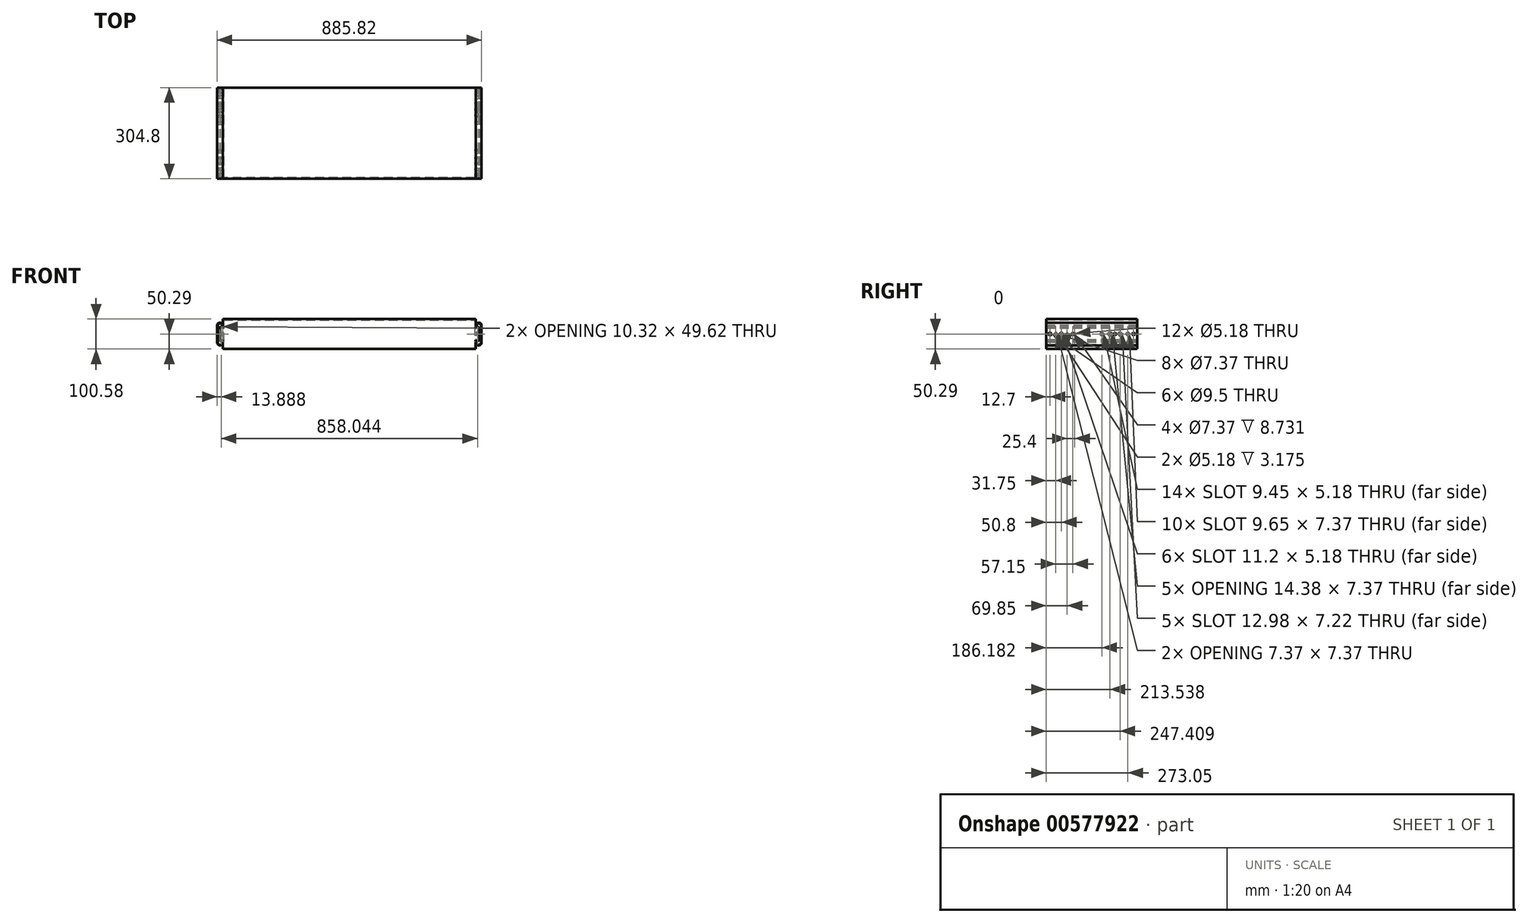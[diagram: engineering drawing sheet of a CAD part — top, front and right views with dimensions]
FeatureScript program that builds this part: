
annotation { "Feature Type Name" : "Feature", "Feature Type Description" : "" }
export const myFeature = defineFeature(function(context is Context, id is Id, definition is map)
    precondition{}
    {
        {
            var Q0;
            Q0=qCreatedBy(makeId("Front.planeOp"),FACE);
            var sketch = newSketch(context, id + "F0", { "sketchPlane" : qUnion([Q0])});
            skLineSegment(sketch, "E0", {"start": v(-442.91, 0) * mm, "end": v(442.91, 0) * mm, "construction": true});
            skLineSegment(sketch, "E1", {"start": v(-442.91, 9.53) * mm, "end": v(-442.91, 66.67) * mm});
            skArc(sketch, "E2", {"start": v(-442.91, 9.53) * mm, "mid": v(-433.39, 0) * mm, "end": v(-423.86, 9.53) * mm});
            skArc(sketch, "E3", {"start": v(-423.86, 66.67) * mm, "mid": v(-433.39, 76.2) * mm, "end": v(-442.91, 66.67) * mm});
            skLineSegment(sketch, "E4", {"start": v(-424.7, 66.67) * mm, "end": v(-423.86, 66.67) * mm, "construction": true});
            skLineSegment(sketch, "E5", {"start": v(-442.91, 9.53) * mm, "end": v(-423.86, 9.53) * mm, "construction": true});
            skArc(sketch, "E6.0", {"start": v(-441.33, 9.53) * mm, "mid": v(-433.75, 1.6) * mm, "end": v(-425.48, 8.8) * mm});
            skLineSegment(sketch, "E6.1", {"start": v(-441.33, 9.53) * mm, "end": v(-441.33, 66.67) * mm});
            skArc(sketch, "E6.2", {"start": v(-425.48, 67.4) * mm, "mid": v(-433.75, 74.6) * mm, "end": v(-441.33, 66.67) * mm});
            skLineSegment(sketch, "E7", {"start": v(-424.7, 9.53) * mm, "end": v(-423.86, 9.53) * mm});
            skLineSegment(sketch, "E8", {"start": v(-425.45, 66.67) * mm, "end": v(-423.86, 66.67) * mm});
            skArc(sketch, "E9.0", {"start": v(-440.53, 9.52) * mm, "mid": v(-433.39, 2.38) * mm, "end": v(-426.24, 9.53) * mm});
            skLineSegment(sketch, "E9.1", {"start": v(-440.53, 9.52) * mm, "end": v(-440.53, 66.67) * mm});
            skArc(sketch, "E9.2", {"start": v(-426.24, 66.67) * mm, "mid": v(-433.39, 73.82) * mm, "end": v(-440.53, 66.67) * mm});
            skLineSegment(sketch, "E10", {"start": v(-426.24, 66.67) * mm, "end": v(-426.24, 66.67) * mm});
            skLineSegment(sketch, "E11", {"start": v(-422.28, 56.97) * mm, "end": v(-422.28, 19.23) * mm, "construction": true});
            skLineSegment(sketch, "E12", {"start": v(-422.28, 10.32) * mm, "end": v(-425.45, 10.32) * mm});
            skLineSegment(sketch, "E13", {"start": v(-426.24, 9.53) * mm, "end": v(-426.24, 9.53) * mm});
            skLineSegment(sketch, "E14", {"start": v(-434.18, 19.23) * mm, "end": v(-434.18, 56.97) * mm});
            skArc(sketch, "E15", {"start": v(-422.28, 56.97) * mm, "mid": v(-428.23, 62.92) * mm, "end": v(-434.18, 56.97) * mm});
            skArc(sketch, "E16", {"start": v(-434.18, 19.23) * mm, "mid": v(-428.23, 13.28) * mm, "end": v(-422.28, 19.23) * mm});
            skLineSegment(sketch, "E17", {"start": v(-440.53, 38.1) * mm, "end": v(-434.18, 38.1) * mm, "construction": true});
            skLineSegment(sketch, "E18", {"start": v(-425.45, 65.88) * mm, "end": v(-423.86, 65.88) * mm});
            skArc(sketch, "E19.0", {"start": v(-432.6, 19.23) * mm, "mid": v(-428.23, 14.86) * mm, "end": v(-423.86, 19.23) * mm});
            skLineSegment(sketch, "E19.1", {"start": v(-432.6, 19.23) * mm, "end": v(-432.6, 56.97) * mm});
            skArc(sketch, "E19.2", {"start": v(-423.86, 56.97) * mm, "mid": v(-428.23, 61.34) * mm, "end": v(-432.6, 56.97) * mm});
            skLineSegment(sketch, "E20", {"start": v(-423.86, 56.97) * mm, "end": v(-423.86, 19.23) * mm});
            skLineSegment(sketch, "E21", {"start": v(-423.86, 10.32) * mm, "end": v(-423.86, 15.18) * mm});
            skLineSegment(sketch, "E22", {"start": v(-423.86, 65.88) * mm, "end": v(-423.86, 61.02) * mm});
            skPoint(sketch, "E23.visualSharp", {"position": v(-426.24, 65.88) * mm});
            skArc(sketch, "E23.filletArc", {"start": v(-426.24, 66.67) * mm, "mid": v(-426.01, 66.11) * mm, "end": v(-425.45, 65.88) * mm});
            skArc(sketch, "E24.filletArc", {"start": v(-425.48, 67.4) * mm, "mid": v(-425.23, 66.88) * mm, "end": v(-424.7, 66.68) * mm});
            skPoint(sketch, "E25.visualSharp", {"position": v(-425.45, 9.53) * mm});
            skArc(sketch, "E25.filletArc", {"start": v(-424.7, 9.53) * mm, "mid": v(-425.23, 9.32) * mm, "end": v(-425.48, 8.8) * mm});
            skPoint(sketch, "E26.visualSharp", {"position": v(-426.24, 10.32) * mm});
            skArc(sketch, "E26.filletArc", {"start": v(-425.45, 10.32) * mm, "mid": v(-426.01, 10.09) * mm, "end": v(-426.24, 9.53) * mm});
            skSolve(sketch);
        }
        {
            var Q0;
            Q0 = qSketchRegion(id + "F0", true);
            extrude(context, id + "F1", {"entities" : qUnion([Q0]), "oppositeDirection" : true, "depth" : 304.8 * mm, "offsetDistance" : 25.4 * mm});
        }
        {
            var Q0;
            Q0=makeQuery(id+"F1.opExtrude","SWEPT_FACE",FACE,{"disambiguationData":[OSD([sQuery(id+"F0.wireOp",EDGE,"E20")])]});
            var sketch = newSketch(context, id + "F2", { "sketchPlane" : qUnion([Q0])});
            skPoint(sketch, "E27", {"position": v(304.8, 38.1) * mm});
            skLineSegment(sketch, "E28", {"start": v(50.8, 35.1) * mm, "end": v(50.8, 41.1) * mm});
            skLineSegment(sketch, "E29", {"start": v(208.94, 38.1) * mm, "end": v(213.2, 38.1) * mm});
            skLineSegment(sketch, "E30", {"start": v(228, 38.1) * mm, "end": v(232.26, 38.1) * mm});
            skLineSegment(sketch, "E31", {"start": v(251.3, 38.1) * mm, "end": v(247.04, 38.1) * mm});
            skPoint(sketch, "E32", {"position": v(50.8, 38.1) * mm});
            skArc(sketch, "E33.0.startCap", {"start": v(53.4, 35.1) * mm, "mid": v(50.8, 32.5) * mm, "end": v(48.2, 35.1) * mm});
            skArc(sketch, "E33.0.endCap", {"start": v(48.2, 41.1) * mm, "mid": v(50.8, 43.7) * mm, "end": v(53.4, 41.1) * mm});
            skLineSegment(sketch, "E33.0.left", {"start": v(48.2, 35.1) * mm, "end": v(48.2, 41.1) * mm});
            skLineSegment(sketch, "E33.0.right", {"start": v(53.4, 35.1) * mm, "end": v(53.4, 41.1) * mm});
            skLineSegment(sketch, "E34", {"start": v(188.32, 38.1) * mm, "end": v(184.05, 38.1) * mm});
            skArc(sketch, "E35.0.startCap", {"start": v(188.32, 40.7) * mm, "mid": v(190.9, 38.1) * mm, "end": v(188.32, 35.5) * mm});
            skArc(sketch, "E35.0.endCap", {"start": v(184.05, 35.5) * mm, "mid": v(181.46, 38.1) * mm, "end": v(184.05, 40.7) * mm});
            skLineSegment(sketch, "E35.0.left", {"start": v(188.32, 35.5) * mm, "end": v(184.05, 35.5) * mm});
            skLineSegment(sketch, "E35.0.right", {"start": v(188.32, 40.7) * mm, "end": v(184.05, 40.7) * mm});
            skArc(sketch, "E35.1.startCap", {"start": v(208.94, 35.5) * mm, "mid": v(206.35, 38.1) * mm, "end": v(208.94, 40.7) * mm});
            skArc(sketch, "E35.1.endCap", {"start": v(213.2, 40.7) * mm, "mid": v(215.8, 38.1) * mm, "end": v(213.2, 35.5) * mm});
            skLineSegment(sketch, "E35.1.left", {"start": v(208.94, 40.7) * mm, "end": v(213.2, 40.7) * mm});
            skLineSegment(sketch, "E35.1.right", {"start": v(208.94, 35.5) * mm, "end": v(213.2, 35.5) * mm});
            skArc(sketch, "E35.2.startCap", {"start": v(228, 35.5) * mm, "mid": v(225.4, 38.1) * mm, "end": v(228, 40.7) * mm});
            skArc(sketch, "E35.2.endCap", {"start": v(232.26, 40.7) * mm, "mid": v(234.85, 38.1) * mm, "end": v(232.26, 35.5) * mm});
            skLineSegment(sketch, "E35.2.left", {"start": v(228, 40.7) * mm, "end": v(232.26, 40.7) * mm});
            skLineSegment(sketch, "E35.2.right", {"start": v(228, 35.5) * mm, "end": v(232.26, 35.5) * mm});
            skArc(sketch, "E35.3.startCap", {"start": v(251.3, 40.7) * mm, "mid": v(253.9, 38.1) * mm, "end": v(251.3, 35.5) * mm});
            skArc(sketch, "E35.3.endCap", {"start": v(247.04, 35.5) * mm, "mid": v(244.45, 38.1) * mm, "end": v(247.04, 40.7) * mm});
            skLineSegment(sketch, "E35.3.left", {"start": v(251.3, 35.5) * mm, "end": v(247.04, 35.5) * mm});
            skLineSegment(sketch, "E35.3.right", {"start": v(251.3, 40.7) * mm, "end": v(247.04, 40.7) * mm});
            skPoint(sketch, "E36", {"position": v(186.18, 38.1) * mm});
            skPoint(sketch, "E37", {"position": v(211.07, 38.1) * mm});
            skPoint(sketch, "E38", {"position": v(230.12, 38.1) * mm});
            skPoint(sketch, "E39", {"position": v(249.17, 38.1) * mm});
            skCircle(sketch, "E40", {"center": v(31.75, 38.1) * mm, "radius": 2.6 * mm});
            skCircle(sketch, "E41", {"center": v(69.85, 38.1) * mm, "radius": 2.6 * mm});
            skCircle(sketch, "E42", {"center": v(95.25, 38.1) * mm, "radius": 2.6 * mm});
            skCircle(sketch, "E43", {"center": v(12.7, 38.1) * mm, "radius": 4.75 * mm});
            skSolve(sketch);
        }
        {
            var Q0;
            Q0 = qSketchRegion(id + "F2", true);
            extrude(context, id + "F3", {"entities" : qUnion([Q0]), "operationType" : NewBodyOperationType.REMOVE, "oppositeDirection" : true, "depth" : 25.4 * mm, "offsetDistance" : 25.4 * mm});
        }
        {
            var Q0;
            Q0=makeQuery(id+"F1.opExtrude","SWEPT_FACE",FACE,{"disambiguationData":[OSD([sQuery(id+"F0.wireOp",EDGE,"E1")])]});
            var sketch = newSketch(context, id + "F4", { "sketchPlane" : qUnion([Q0])});
            skCircle(sketch, "E44", {"center": v(-88.9, 38.1) * mm, "radius": 3.68 * mm});
            skPoint(sketch, "E44.centerSnap0", {"position": v(0, 38.1) * mm});
            skCircle(sketch, "E45", {"center": v(-31.75, 38.1) * mm, "radius": 3.68 * mm});
            skCircle(sketch, "E46", {"center": v(-244.6, 38.1) * mm, "radius": 3.68 * mm});
            skLineSegment(sketch, "E47", {"start": v(-293.24, 38.1) * mm, "end": v(-290.96, 38.1) * mm});
            skPoint(sketch, "E47.startSnap0", {"position": v(-304.8, 38.1) * mm});
            skLineSegment(sketch, "E48", {"start": v(-274.2, 38.1) * mm, "end": v(-271.9, 38.1) * mm});
            skLineSegment(sketch, "E49", {"start": v(-217.04, 38.1) * mm, "end": v(-214.76, 38.1) * mm});
            skPoint(sketch, "E50", {"position": v(-292.1, 38.1) * mm});
            skPoint(sketch, "E51", {"position": v(-273.05, 38.1) * mm});
            skPoint(sketch, "E52", {"position": v(-215.9, 38.1) * mm});
            skArc(sketch, "E53.0.startCap", {"start": v(-293.24, 34.42) * mm, "mid": v(-296.93, 38.1) * mm, "end": v(-293.24, 41.78) * mm});
            skArc(sketch, "E53.0.endCap", {"start": v(-290.96, 41.78) * mm, "mid": v(-287.27, 38.1) * mm, "end": v(-290.96, 34.42) * mm});
            skLineSegment(sketch, "E53.0.left", {"start": v(-293.24, 41.78) * mm, "end": v(-290.96, 41.78) * mm});
            skLineSegment(sketch, "E53.0.right", {"start": v(-293.24, 34.42) * mm, "end": v(-290.96, 34.42) * mm});
            skArc(sketch, "E53.1.startCap", {"start": v(-274.2, 34.42) * mm, "mid": v(-277.88, 38.1) * mm, "end": v(-274.2, 41.78) * mm});
            skArc(sketch, "E53.1.endCap", {"start": v(-271.9, 41.78) * mm, "mid": v(-268.22, 38.1) * mm, "end": v(-271.9, 34.42) * mm});
            skLineSegment(sketch, "E53.1.left", {"start": v(-274.2, 41.78) * mm, "end": v(-271.9, 41.78) * mm});
            skLineSegment(sketch, "E53.1.right", {"start": v(-274.2, 34.42) * mm, "end": v(-271.9, 34.42) * mm});
            skArc(sketch, "E53.2.startCap", {"start": v(-217.04, 34.42) * mm, "mid": v(-220.73, 38.1) * mm, "end": v(-217.04, 41.78) * mm});
            skArc(sketch, "E53.2.endCap", {"start": v(-214.76, 41.78) * mm, "mid": v(-211.07, 38.1) * mm, "end": v(-214.76, 34.42) * mm});
            skLineSegment(sketch, "E53.2.left", {"start": v(-217.04, 41.78) * mm, "end": v(-214.76, 41.78) * mm});
            skLineSegment(sketch, "E53.2.right", {"start": v(-217.04, 34.42) * mm, "end": v(-214.76, 34.42) * mm});
            skSolve(sketch);
        }
        {
            var Q0;
            Q0 = qSketchRegion(id + "F4", true);
            extrude(context, id + "F5", {"entities" : qUnion([Q0]), "operationType" : NewBodyOperationType.REMOVE, "oppositeDirection" : true, "depth" : 25.4 * mm, "offsetDistance" : 25.4 * mm});
        }
        {
            var Q0;
            Q0=makeQuery(id+"F1.opExtrude","CAP_FACE",FACE,{"disambiguationData":[OSD([sQuery(id+"F0.wireOp",EDGE,"E19.0"),sQuery(id+"F0.wireOp",EDGE,"E19.1"),sQuery(id+"F0.wireOp",EDGE,"E19.2"),sQuery(id+"F0.wireOp",EDGE,"E20")])],"isStart":true});
            extrude(context, id + "F6", {"entities" : qUnion([Q0]), "operationType" : NewBodyOperationType.REMOVE, "oppositeDirection" : true, "depth" : 3.17 * mm, "offsetDistance" : 25.4 * mm});
        }
        {
            var Q0;
            Q0=makeQuery(id+"F6.boolean.opBoolean","COPY",FACE,{"derivedFrom":makeQuery(id+"F6.opExtrude","CAP_FACE",FACE,{"disambiguationData":[OSD([sQuery(id+"F0.wireOp",EDGE,"E19.0"),sQuery(id+"F0.wireOp",EDGE,"E19.1"),sQuery(id+"F0.wireOp",EDGE,"E19.2"),sQuery(id+"F0.wireOp",EDGE,"E20")])],"isStart":false})});
            extrude(context, id + "F7", {"entities" : qUnion([Q0]), "depth" : 3.17 * mm, "offsetDistance" : 25.4 * mm});
        }
        {
            var Q0;
            Q0=makeQuery(id+"F1.opExtrude","SWEPT_BODY",BODY,{"disambiguationData":[OSD([sQuery(id+"F0.wireOp",EDGE,"E19.0"),sQuery(id+"F0.wireOp",EDGE,"E19.1"),sQuery(id+"F0.wireOp",EDGE,"E19.2"),sQuery(id+"F0.wireOp",EDGE,"E20")])]});
            var Q1;
            Q1=makeQuery(id+"F1.opExtrude","SWEPT_BODY",BODY,{"disambiguationData":[OSD([sQuery(id+"F0.wireOp",EDGE,"E9.0"),sQuery(id+"F0.wireOp",EDGE,"E9.1"),sQuery(id+"F0.wireOp",EDGE,"E9.2"),sQuery(id+"F0.wireOp",EDGE,"E12"),sQuery(id+"F0.wireOp",EDGE,"E14"),sQuery(id+"F0.wireOp",EDGE,"E15"),sQuery(id+"F0.wireOp",EDGE,"E16"),sQuery(id+"F0.wireOp",EDGE,"E18"),sQuery(id+"F0.wireOp",EDGE,"E21"),sQuery(id+"F0.wireOp",EDGE,"E22"),sQuery(id+"F0.wireOp",EDGE,"E23.filletArc"),sQuery(id+"F0.wireOp",EDGE,"E26.filletArc")])]});
            var Q2;
            Q2=makeQuery(id+"F1.opExtrude","SWEPT_BODY",BODY,{"disambiguationData":[OSD([sQuery(id+"F0.wireOp",EDGE,"E1"),sQuery(id+"F0.wireOp",EDGE,"E2"),sQuery(id+"F0.wireOp",EDGE,"E3"),sQuery(id+"F0.wireOp",EDGE,"E6.0"),sQuery(id+"F0.wireOp",EDGE,"E6.1"),sQuery(id+"F0.wireOp",EDGE,"E6.2"),sQuery(id+"F0.wireOp",EDGE,"E7"),sQuery(id+"F0.wireOp",EDGE,"E8"),sQuery(id+"F0.wireOp",EDGE,"E24.filletArc"),sQuery(id+"F0.wireOp",EDGE,"E25.filletArc")])]});
            var Q3;
            Q3=makeQuery(id+"F7.opExtrude","SWEPT_BODY",BODY,{"disambiguationData":[OSD([sQuery(id+"F0.wireOp",EDGE,"E19.0"),sQuery(id+"F0.wireOp",EDGE,"E19.1"),sQuery(id+"F0.wireOp",EDGE,"E19.2"),sQuery(id+"F0.wireOp",EDGE,"E20")])]});
            var Q4;
            Q4=qCreatedBy(makeId("Right.planeOp"),FACE);
            mirror(context, id + "F8", {"entities" : qUnion([Q0, Q1, Q2, Q3]), "mirrorPlane" : qUnion([Q4])});
        }
        {
            var Q0;
            Q0=qCreatedBy(makeId("Front.planeOp"),FACE);
            var sketch = newSketch(context, id + "F9", { "sketchPlane" : qUnion([Q0])});
            skLineSegment(sketch, "E54.bottom", {"start": v(-423.86, 88.4) * mm, "end": v(-420.69, 88.4) * mm});
            skLineSegment(sketch, "E54.top", {"start": v(-423.86, -12.2) * mm, "end": v(-420.69, -12.2) * mm});
            skLineSegment(sketch, "E54.right", {"start": v(-420.69, 88.4) * mm, "end": v(-420.69, -12.2) * mm});
            skLineSegment(sketch, "E55.top", {"start": v(-423.86, -9.02) * mm, "end": v(-420.69, -9.02) * mm});
            skLineSegment(sketch, "E55.left", {"start": v(-423.86, -12.2) * mm, "end": v(-423.86, -9.02) * mm});
            skLineSegment(sketch, "E55.right", {"start": v(423.86, -12.2) * mm, "end": v(423.86, -9.02) * mm});
            skLineSegment(sketch, "E56.bottom", {"start": v(423.86, -12.2) * mm, "end": v(420.69, -12.2) * mm});
            skLineSegment(sketch, "E56.top", {"start": v(423.86, 88.4) * mm, "end": v(420.69, 88.4) * mm});
            skLineSegment(sketch, "E56.left", {"start": v(423.86, -12.2) * mm, "end": v(423.86, 88.4) * mm});
            skLineSegment(sketch, "E56.right", {"start": v(420.69, -12.2) * mm, "end": v(420.69, 88.4) * mm});
            skLineSegment(sketch, "E57", {"start": v(-423.86, 88.4) * mm, "end": v(-423.86, -12.2) * mm});
            skLineSegment(sketch, "E58.0.0", {"start": v(-423.86, 19.23) * mm, "end": v(-423.86, 56.97) * mm});
            skLineSegment(sketch, "E58.0.2", {"start": v(-432.6, 56.97) * mm, "end": v(-432.6, 19.23) * mm});
            skArc(sketch, "E58.0.3", {"start": v(-432.6, 19.23) * mm, "mid": v(-428.23, 14.86) * mm, "end": v(-423.86, 19.23) * mm});
            skPoint(sketch, "E59", {"position": v(-423.86, 38.1) * mm});
            skLineSegment(sketch, "E60.bottom", {"start": v(-423.86, 88.4) * mm, "end": v(423.86, 88.4) * mm});
            skLineSegment(sketch, "E60.top", {"start": v(-423.86, 85.22) * mm, "end": v(423.86, 85.22) * mm});
            skLineSegment(sketch, "E60.left", {"start": v(-423.86, 88.4) * mm, "end": v(-423.86, 85.22) * mm});
            skLineSegment(sketch, "E60.right", {"start": v(423.86, 88.4) * mm, "end": v(423.86, 85.22) * mm});
            skLineSegment(sketch, "E61.trimOffspring", {"start": v(420.69, -12.2) * mm, "end": v(423.86, -12.2) * mm});
            skLineSegment(sketch, "E62.trimOffspring", {"start": v(420.69, -9.02) * mm, "end": v(423.86, -9.02) * mm});
            skSolve(sketch);
        }
        {
            var Q0;
            Q0 = qSketchRegion(id + "F9", true);
            extrude(context, id + "F10", {"entities" : qUnion([Q0]), "oppositeDirection" : true, "depth" : 304.8 * mm, "offsetDistance" : 25.4 * mm});
        }
        {
            var Q0;
            Q0=makeQuery(id+"F10.opExtrude","SWEPT_FACE",FACE,{"disambiguationData":[OSD([sQuery(id+"F9.wireOp",EDGE,"E54.right")])]});
            var sketch = newSketch(context, id + "F11", { "sketchPlane" : qUnion([Q0])});
            skPoint(sketch, "E63.0", {"position": v(304.8, 38.1) * mm});
            skLineSegment(sketch, "E63.1", {"start": v(50.8, 35.1) * mm, "end": v(50.8, 41.1) * mm});
            skLineSegment(sketch, "E63.2", {"start": v(208.94, 38.1) * mm, "end": v(213.2, 38.1) * mm});
            skLineSegment(sketch, "E63.3", {"start": v(228, 38.1) * mm, "end": v(232.26, 38.1) * mm});
            skLineSegment(sketch, "E63.4", {"start": v(251.3, 38.1) * mm, "end": v(247.04, 38.1) * mm});
            skPoint(sketch, "E63.5", {"position": v(50.8, 38.1) * mm});
            skArc(sketch, "E63.6", {"start": v(53.4, 35.1) * mm, "mid": v(50.8, 32.5) * mm, "end": v(48.2, 35.1) * mm});
            skArc(sketch, "E63.7", {"start": v(48.2, 41.1) * mm, "mid": v(50.8, 43.7) * mm, "end": v(53.4, 41.1) * mm});
            skLineSegment(sketch, "E63.8", {"start": v(48.2, 35.1) * mm, "end": v(48.2, 41.1) * mm});
            skLineSegment(sketch, "E63.9", {"start": v(53.4, 35.1) * mm, "end": v(53.4, 41.1) * mm});
            skLineSegment(sketch, "E63.10", {"start": v(188.32, 38.1) * mm, "end": v(184.05, 38.1) * mm});
            skArc(sketch, "E63.11", {"start": v(188.32, 40.7) * mm, "mid": v(190.9, 38.1) * mm, "end": v(188.32, 35.5) * mm});
            skArc(sketch, "E63.12", {"start": v(184.05, 35.5) * mm, "mid": v(181.46, 38.1) * mm, "end": v(184.05, 40.7) * mm});
            skLineSegment(sketch, "E63.13", {"start": v(188.32, 35.5) * mm, "end": v(184.05, 35.5) * mm});
            skLineSegment(sketch, "E63.14", {"start": v(188.32, 40.7) * mm, "end": v(184.05, 40.7) * mm});
            skArc(sketch, "E63.15", {"start": v(208.94, 35.5) * mm, "mid": v(206.35, 38.1) * mm, "end": v(208.94, 40.7) * mm});
            skArc(sketch, "E63.16", {"start": v(213.2, 40.7) * mm, "mid": v(215.8, 38.1) * mm, "end": v(213.2, 35.5) * mm});
            skLineSegment(sketch, "E63.17", {"start": v(208.94, 40.7) * mm, "end": v(213.2, 40.7) * mm});
            skLineSegment(sketch, "E63.18", {"start": v(208.94, 35.5) * mm, "end": v(213.2, 35.5) * mm});
            skArc(sketch, "E63.19", {"start": v(228, 35.5) * mm, "mid": v(225.4, 38.1) * mm, "end": v(228, 40.7) * mm});
            skArc(sketch, "E63.20", {"start": v(232.26, 40.7) * mm, "mid": v(234.85, 38.1) * mm, "end": v(232.26, 35.5) * mm});
            skLineSegment(sketch, "E63.21", {"start": v(228, 40.7) * mm, "end": v(232.26, 40.7) * mm});
            skLineSegment(sketch, "E63.22", {"start": v(228, 35.5) * mm, "end": v(232.26, 35.5) * mm});
            skArc(sketch, "E63.23", {"start": v(251.3, 40.7) * mm, "mid": v(253.9, 38.1) * mm, "end": v(251.3, 35.5) * mm});
            skArc(sketch, "E63.24", {"start": v(247.04, 35.5) * mm, "mid": v(244.45, 38.1) * mm, "end": v(247.04, 40.7) * mm});
            skLineSegment(sketch, "E63.25", {"start": v(251.3, 35.5) * mm, "end": v(247.04, 35.5) * mm});
            skLineSegment(sketch, "E63.26", {"start": v(251.3, 40.7) * mm, "end": v(247.04, 40.7) * mm});
            skPoint(sketch, "E63.27", {"position": v(186.18, 38.1) * mm});
            skPoint(sketch, "E63.28", {"position": v(211.07, 38.1) * mm});
            skPoint(sketch, "E63.29", {"position": v(230.12, 38.1) * mm});
            skPoint(sketch, "E63.30", {"position": v(249.17, 38.1) * mm});
            skCircle(sketch, "E63.31", {"center": v(31.75, 38.1) * mm, "radius": 2.6 * mm});
            skCircle(sketch, "E63.32", {"center": v(69.85, 38.1) * mm, "radius": 2.6 * mm});
            skCircle(sketch, "E63.33", {"center": v(95.25, 38.1) * mm, "radius": 2.6 * mm});
            skCircle(sketch, "E63.34", {"center": v(12.7, 38.1) * mm, "radius": 4.75 * mm});
            skSolve(sketch);
        }
        {
            var Q0;
            Q0 = qSketchRegion(id + "F11", true);
            extrude(context, id + "F12", {"entities" : qUnion([Q0]), "operationType" : NewBodyOperationType.REMOVE, "endBound" : BoundingType.THROUGH_ALL, "oppositeDirection" : true, "depth" : 25.4 * mm, "offsetDistance" : 25.4 * mm, "hasSecondDirection" : true, "secondDirectionBound" : BoundingType.THROUGH_ALL, "secondDirectionOppositeDirection" : false, "secondDirectionDepth" : 25.4 * mm});
        }
        {
            var Q0;
            Q0=makeQuery(id+"F10.opExtrude","CAP_FACE",FACE,{"disambiguationData":[OSD([sQuery(id+"F9.wireOp",EDGE,"E54.right"),sQuery(id+"F9.wireOp",EDGE,"E54.top"),sQuery(id+"F9.wireOp",EDGE,"E56.left"),sQuery(id+"F9.wireOp",EDGE,"E56.right"),sQuery(id+"F9.wireOp",EDGE,"E57"),sQuery(id+"F9.wireOp",EDGE,"E58.0.0"),sQuery(id+"F9.wireOp",EDGE,"E60.bottom"),sQuery(id+"F9.wireOp",EDGE,"E60.top"),sQuery(id+"F9.wireOp",EDGE,"E60.left"),sQuery(id+"F9.wireOp",EDGE,"E60.right"),sQuery(id+"F9.wireOp",EDGE,"E61.trimOffspring")])],"isStart":true});
            var sketch = newSketch(context, id + "F13", { "sketchPlane" : qUnion([Q0])});
            skLineSegment(sketch, "E64.bottom", {"start": v(-423.86, 88.4) * mm, "end": v(423.86, 88.4) * mm});
            skLineSegment(sketch, "E64.top", {"start": v(-423.86, -12.2) * mm, "end": v(423.86, -12.2) * mm});
            skLineSegment(sketch, "E64.left", {"start": v(-423.86, 88.4) * mm, "end": v(-423.86, -12.2) * mm});
            skLineSegment(sketch, "E64.right", {"start": v(423.86, 88.4) * mm, "end": v(423.86, -12.2) * mm});
            skSolve(sketch);
        }
        {
            var Q0;
            Q0 = qSketchRegion(id + "F13", true);
            extrude(context, id + "F14", {"entities" : qUnion([Q0]), "operationType" : NewBodyOperationType.ADD, "oppositeDirection" : true, "depth" : 3.17 * mm, "offsetDistance" : 25.4 * mm});
        }
    });
